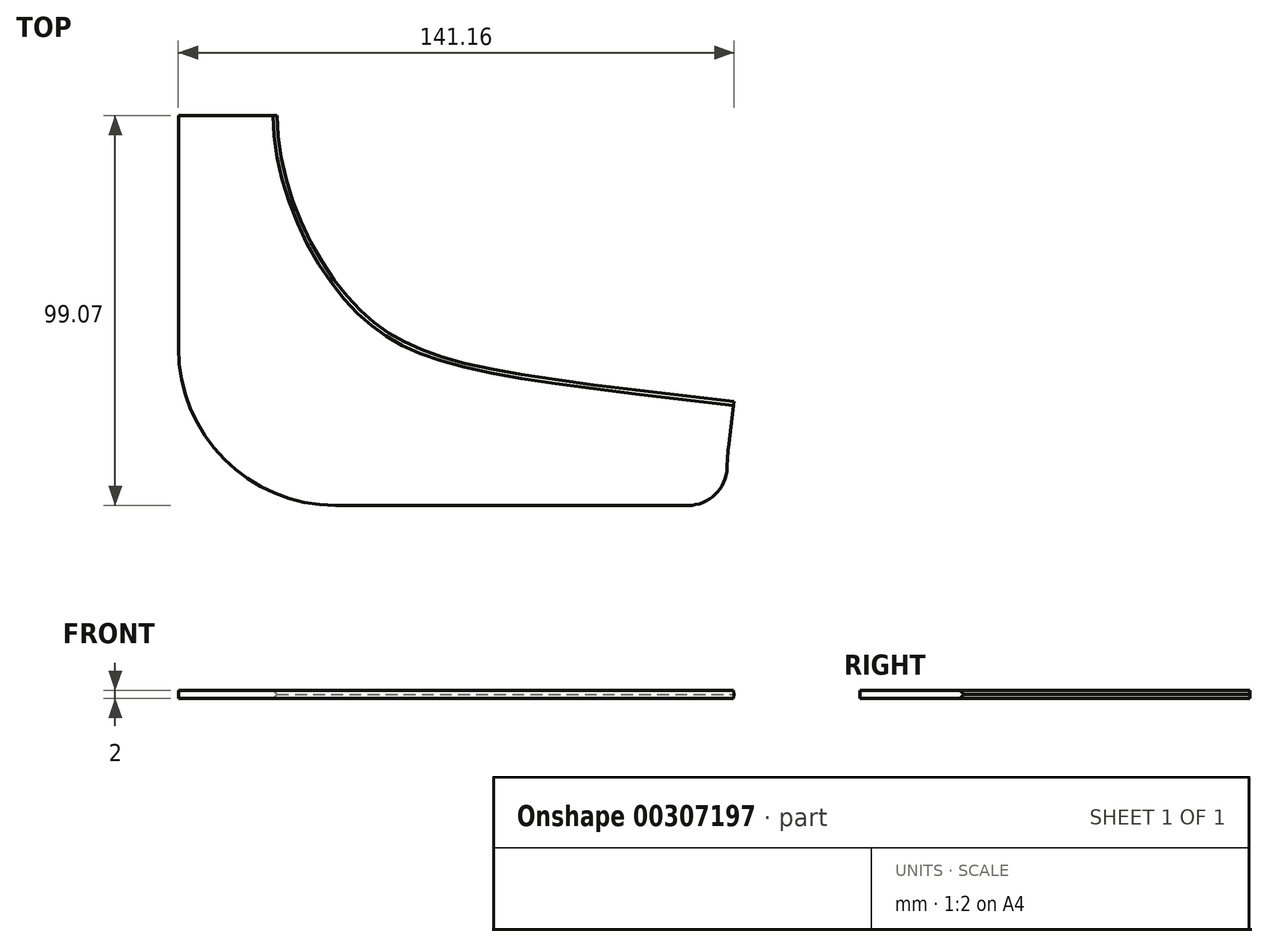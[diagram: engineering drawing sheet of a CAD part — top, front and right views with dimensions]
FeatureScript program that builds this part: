
annotation { "Feature Type Name" : "Feature", "Feature Type Description" : "" }
export const myFeature = defineFeature(function(context is Context, id is Id, definition is map)
    precondition{}
    {
        {
            var Q0;
            Q0=qCreatedBy(makeId("Top.planeOp"),FACE);
            var sketch = newSketch(context, id + "F0", { "sketchPlane" : qUnion([Q0])});
            skFitSpline(sketch, "E0", {"points": [v(0, 0) * mm, v(25.33, -58.84) * mm, v(127.1, -85.1) * mm], "startDerivative": vector(0, -145.1) * mm, "endDerivative": vector(313.7, -37.8) * mm});
            skSolve(sketch);
        }
        {
            var Q0;
            Q0=qCreatedBy(makeId("Front.planeOp"),FACE);
            var sketch = newSketch(context, id + "F1", { "sketchPlane" : qUnion([Q0])});
            skEllipse(sketch, "E1", {"center": v(0, 0) * mm, "majorRadius": 12.5 * mm, "minorRadius": 1 * mm, "majorAxis": v(-1, 0)});
            skLineSegment(sketch, "E2", {"start": v(0, -1) * mm, "end": v(11.5, -1) * mm});
            skLineSegment(sketch, "E3", {"start": v(11.5, -1) * mm, "end": v(12.5, 0) * mm});
            skLineSegment(sketch, "E4", {"start": v(12.5, 0) * mm, "end": v(12.5, 0) * mm});
            skLineSegment(sketch, "E5", {"start": v(0, 1) * mm, "end": v(11.5, 1) * mm});
            skLineSegment(sketch, "E6", {"start": v(11.5, 1) * mm, "end": v(12.5, 0) * mm});
            skLineSegment(sketch, "E7", {"start": v(0, 1) * mm, "end": v(-6, 1) * mm});
            skLineSegment(sketch, "E8", {"start": v(-6, 1) * mm, "end": v(-12.5, 0) * mm});
            skLineSegment(sketch, "E9", {"start": v(-6, -1) * mm, "end": v(-12.5, 0) * mm});
            skLineSegment(sketch, "E10", {"start": v(-6, -1) * mm, "end": v(0, -1) * mm});
            skLineSegment(sketch, "E11", {"start": v(0, -1) * mm, "end": v(0, 1) * mm});
            skSolve(sketch);
        }
        {
            var Q0;
            {var subQ6=sQuery(id+"F1.wireOp",EDGE,"E11");Q0=makeQuery(id+"F1.imprint","IMPRINT",FACE,{"disambiguationData":[TD([[makeQuery(id+"F1.imprint","IMPRINT",EDGE,{"derivedFrom":subQ6}),1.0]])]});}
            var Q1;
            {var subQ4=sQuery(id+"F1.wireOp",EDGE,"E11");Q1=makeQuery(id+"F1.imprint","IMPRINT",FACE,{"disambiguationData":[TD([[makeQuery(id+"F1.imprint","IMPRINT",EDGE,{"derivedFrom":subQ4}),-1.0]])]});}
            var Q2;
            {var subQ0=sQuery(id+"F1.wireOp",EDGE,"E10");Q2=makeQuery(id+"F1.imprint","IMPRINT",FACE,{"disambiguationData":[TD([[makeQuery(id+"F1.imprint","IMPRINT",EDGE,{"derivedFrom":subQ0}),1.0]])]});}
            var Q3;
            {var subQ0=sQuery(id+"F1.wireOp",EDGE,"E7");Q3=makeQuery(id+"F1.imprint","IMPRINT",FACE,{"disambiguationData":[TD([[makeQuery(id+"F1.imprint","IMPRINT",EDGE,{"derivedFrom":subQ0}),1.0]])]});}
            var Q4;
            {var subQ0=sQuery(id+"F1.wireOp",EDGE,"E5");Q4=makeQuery(id+"F1.imprint","IMPRINT",FACE,{"disambiguationData":[TD([[makeQuery(id+"F1.imprint","IMPRINT",EDGE,{"derivedFrom":subQ0}),-1.0]])]});}
            var Q5;
            {var subQ0=sQuery(id+"F1.wireOp",EDGE,"E2");Q5=makeQuery(id+"F1.imprint","IMPRINT",FACE,{"disambiguationData":[TD([[makeQuery(id+"F1.imprint","IMPRINT",EDGE,{"derivedFrom":subQ0}),1.0]])]});}
            var Q6;
            Q6=sQuery(id+"F0.wireOp",EDGE,"E0");
            sweep(context, id + "F2", {"profiles" : qUnion([Q0, Q1, Q2, Q3, Q4, Q5]), "path" : qUnion([Q6])});
        }
        {
            var Q0;
            Q0=qCreatedBy(makeId("Top.planeOp"),FACE);
            var sketch = newSketch(context, id + "F3", { "sketchPlane" : qUnion([Q0])});
            skFitSpline(sketch, "E12", {"points": [v(0, 0) * mm, v(25.29, -58.84) * mm, v(127.05, -85.1) * mm], "startDerivative": vector(0, -145.1) * mm, "endDerivative": vector(313.7, -37.8) * mm});
            skLineSegment(sketch, "E13", {"start": v(0, 0) * mm, "end": v(-12.56, 0) * mm});
            skLineSegment(sketch, "E14", {"start": v(-12.56, 0) * mm, "end": v(-12.56, -99.07) * mm});
            skLineSegment(sketch, "E15", {"start": v(-12.56, -99.07) * mm, "end": v(126.52, -99.07) * mm});
            skLineSegment(sketch, "E16", {"start": v(126.52, -99.07) * mm, "end": v(127.05, -85.1) * mm});
            skSolve(sketch);
        }
        {
            var Q0;
            Q0=qSketchRegion(id+"F3",true);
            extrude(context, id + "F4", {"entities" : qUnion([Q0]), "operationType" : NewBodyOperationType.ADD, "endBound" : BoundingType.SYMMETRIC, "depth" : 2 * mm});
        }
        {
            var Q0;
            Q0=makeQuery(id+"F4.boolean.opBoolean","INTERSECT",EDGE,{"derivedFrom":[makeQuery(id+"F2.opSweep","CAP_FACE",FACE,{"disambiguationData":[OSD([sQuery(id+"F0.wireOp",VERTEX,"E0.end"),sQuery(id+"F1.wireOp",EDGE,"E1")])],"isStart":false}),makeQuery(id+"F4.opExtrude","SWEPT_FACE",FACE,{"disambiguationData":[OSD([sQuery(id+"F3.wireOp",EDGE,"E16")])]})]});
            fillet(context, id + "F5", {"entities" : qUnion([Q0]), "radius" : 30 * mm, "tangentPropagation" : true, "allowEdgeOverflow" : false});
        }
        {
            var Q0;
            Q0=makeQuery(id+"F4.opExtrude","SWEPT_EDGE",EDGE,{"disambiguationData":[OSD([sQuery(id+"F3.wireOp",EDGE,"E15"),sQuery(id+"F3.wireOp",EDGE,"E16")])]});
            fillet(context, id + "F6", {"entities" : qUnion([Q0]), "radius" : 10 * mm, "tangentPropagation" : true, "allowEdgeOverflow" : false});
        }
        {
            var Q0;
            Q0=makeQuery(id+"F4.opExtrude","SWEPT_EDGE",EDGE,{"disambiguationData":[OSD([sQuery(id+"F3.wireOp",EDGE,"E14"),sQuery(id+"F3.wireOp",EDGE,"E15")])]});
            fillet(context, id + "F7", {"entities" : qUnion([Q0]), "radius" : 40 * mm, "tangentPropagation" : true, "allowEdgeOverflow" : false});
        }
    });
